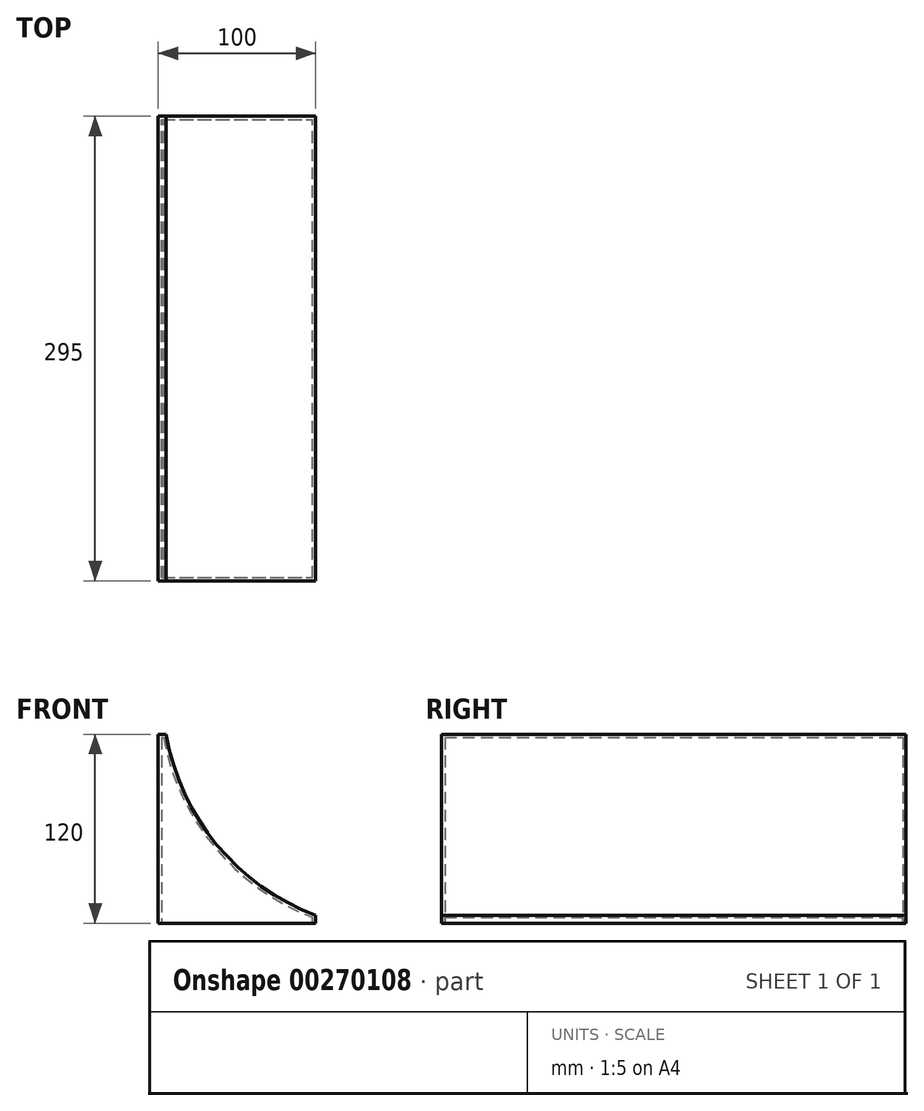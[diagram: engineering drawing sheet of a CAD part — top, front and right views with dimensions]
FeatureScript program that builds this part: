
annotation { "Feature Type Name" : "Feature", "Feature Type Description" : "" }
export const myFeature = defineFeature(function(context is Context, id is Id, definition is map)
    precondition{}
    {
        {
            var Q0;
            Q0=qCreatedBy(makeId("Front.planeOp"),FACE);
            var sketch = newSketch(context, id + "F0", { "sketchPlane" : qUnion([Q0])});
            skLineSegment(sketch, "E0", {"start": v(-100, 120) * mm, "end": v(-100, 0) * mm});
            skLineSegment(sketch, "E1", {"start": v(-100, 0) * mm, "end": v(0, 0) * mm});
            skLineSegment(sketch, "E2", {"start": v(-100, 120) * mm, "end": v(-95, 120) * mm});
            skLineSegment(sketch, "E3", {"start": v(0, 0) * mm, "end": v(0, 5) * mm});
            skArc(sketch, "E4", {"start": v(-95, 120) * mm, "mid": v(-62.8, 49.85) * mm, "end": v(0, 5) * mm});
            skSolve(sketch);
        }
        {
            var Q0;
            Q0 = qSketchRegion(id + "F0", true);
            extrude(context, id + "F1", {"entities" : qUnion([Q0]), "depth" : 295 * mm, "symmetric" : true});
        }
        {
            var Q0;
            Q0=makeQuery(id+"F1.opExtrude","SWEPT_FACE",FACE,{"disambiguationData":[OSD([sQuery(id+"F0.wireOp",EDGE,"E1")])]});
            shell(context, id + "F2", {"entities" : qUnion([Q0]), "thickness" : 2 * mm});
        }
    });
